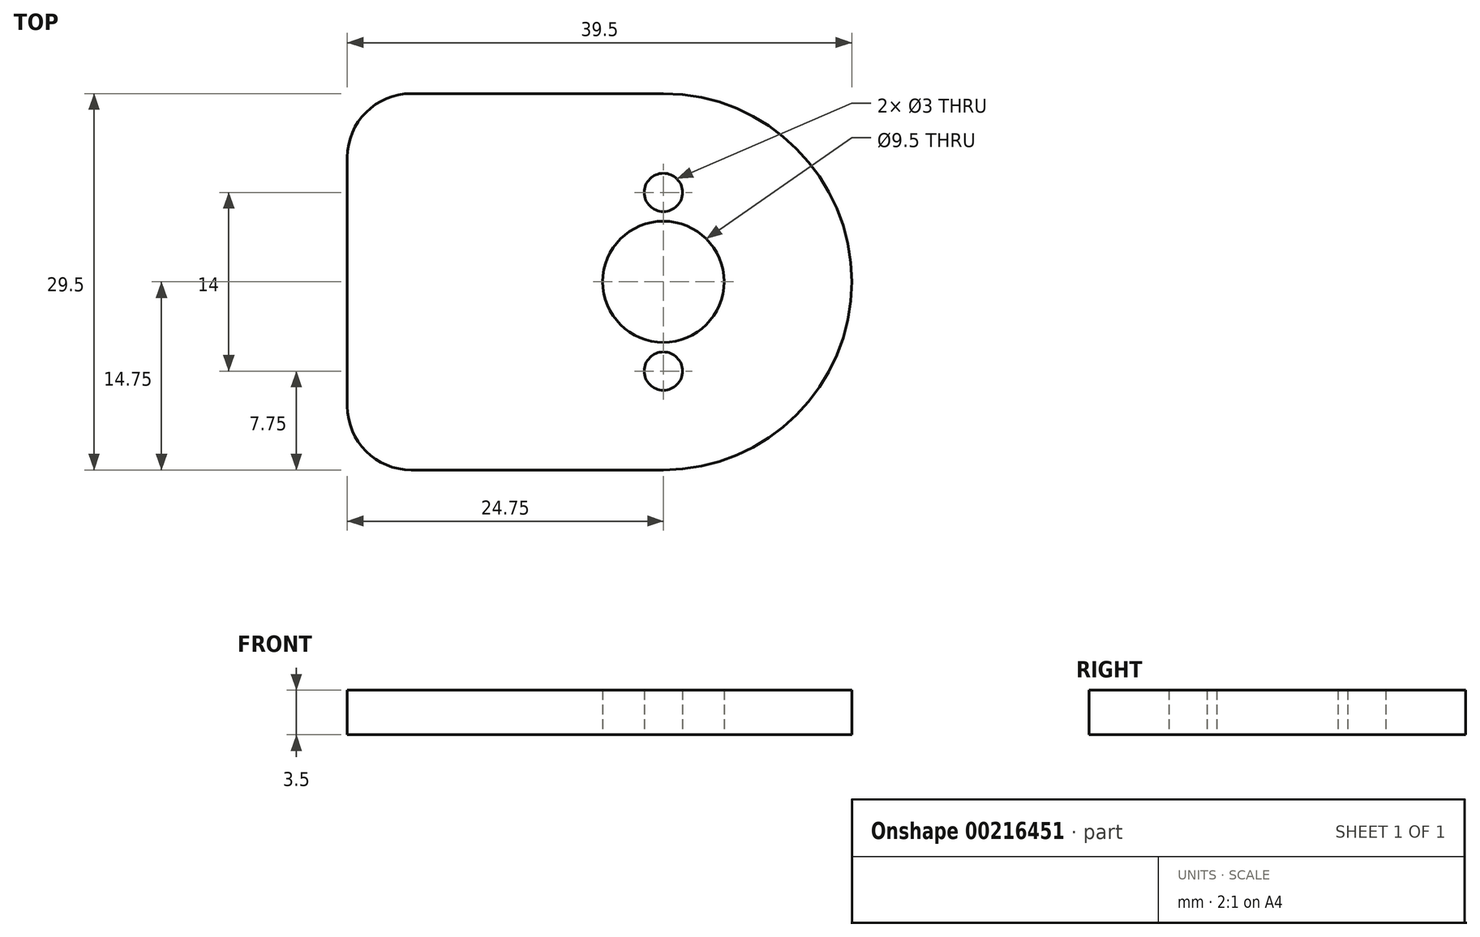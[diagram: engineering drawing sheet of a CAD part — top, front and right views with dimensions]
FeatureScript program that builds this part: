
annotation { "Feature Type Name" : "Feature", "Feature Type Description" : "" }
export const myFeature = defineFeature(function(context is Context, id is Id, definition is map)
    precondition{}
    {
        {
            var Q0;
            Q0=qCreatedBy(makeId("Top.planeOp"),FACE);
            var sketch = newSketch(context, id + "F0", { "sketchPlane" : qUnion([Q0])});
            skCircle(sketch, "E0", {"center": v(0, 0) * mm, "radius": 4.75 * mm});
            skArc(sketch, "E1", {"start": v(0, -14.75) * mm, "mid": v(14.75, 0) * mm, "end": v(0, 14.75) * mm});
            skLineSegment(sketch, "E2", {"start": v(0, 14.75) * mm, "end": v(-19.75, 14.75) * mm});
            skLineSegment(sketch, "E3", {"start": v(-24.75, 9.75) * mm, "end": v(-24.75, -9.75) * mm});
            skLineSegment(sketch, "E4.MirrorCS", {"start": v(0, -14.75) * mm, "end": v(-19.75, -14.75) * mm});
            skPoint(sketch, "E5.visualSharp", {"position": v(-24.75, 14.75) * mm});
            skArc(sketch, "E5.filletArc", {"start": v(-19.75, 14.75) * mm, "mid": v(-23.29, 13.29) * mm, "end": v(-24.75, 9.75) * mm});
            skPoint(sketch, "E6.visualSharp", {"position": v(-24.75, -14.75) * mm});
            skArc(sketch, "E6.filletArc", {"start": v(-24.75, -9.75) * mm, "mid": v(-23.29, -13.29) * mm, "end": v(-19.75, -14.75) * mm});
            skCircle(sketch, "E7", {"center": v(0, -7) * mm, "radius": 1.5 * mm});
            skCircle(sketch, "E8.MirrorC", {"center": v(0, 7) * mm, "radius": 1.5 * mm});
            skSolve(sketch);
        }
        {
            var Q0;
            Q0 = qSketchRegion(id + "F0", true);
            extrude(context, id + "F1", {"entities" : qUnion([Q0]), "depth" : 3.5 * mm});
        }
    });
